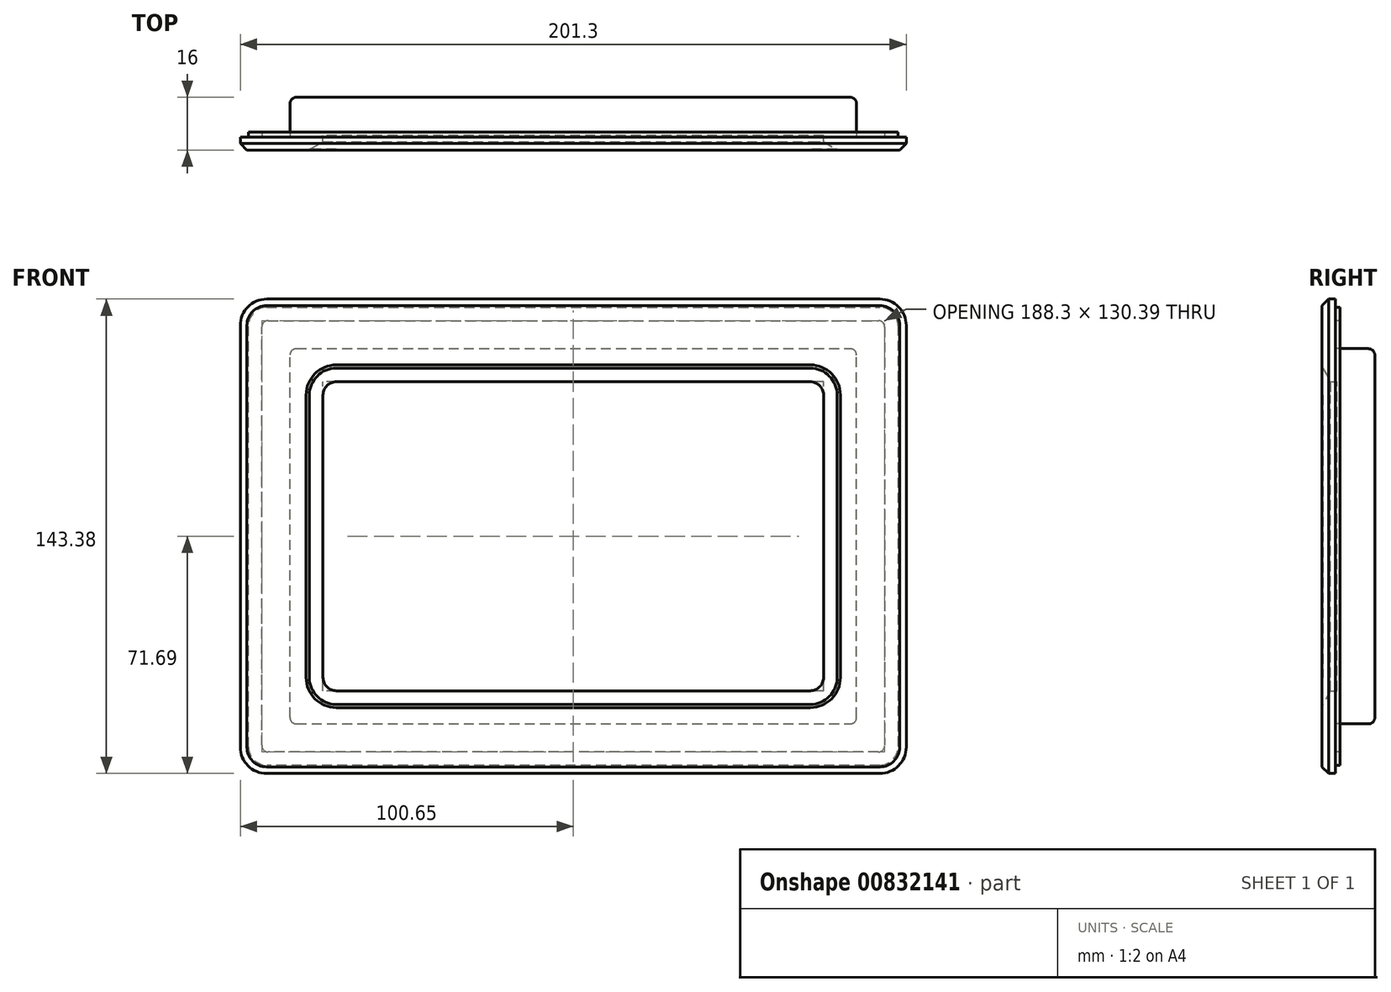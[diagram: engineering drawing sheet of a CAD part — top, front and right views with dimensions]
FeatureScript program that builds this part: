
annotation { "Feature Type Name" : "Feature", "Feature Type Description" : "" }
export const myFeature = defineFeature(function(context is Context, id is Id, definition is map)
    precondition{}
    {
        {
            var Q0;
            Q0=qCreatedBy(makeId("Front.planeOp"),FACE);
            var sketch = newSketch(context, id + "F0", { "sketchPlane" : qUnion([Q0])});
            skLineSegment(sketch, "E0.bottom", {"start": v(75.65, -46.7) * mm, "end": v(-75.65, -46.7) * mm});
            skLineSegment(sketch, "E0.top", {"start": v(75.65, 46.7) * mm, "end": v(-75.65, 46.7) * mm});
            skLineSegment(sketch, "E0.left", {"start": v(75.65, -46.7) * mm, "end": v(75.65, 46.7) * mm});
            skLineSegment(sketch, "E0.right", {"start": v(-75.65, -46.7) * mm, "end": v(-75.65, 46.7) * mm});
            skPoint(sketch, "E0.middle", {"position": v(0, 0) * mm});
            skSolve(sketch);
        }
        {
            var Q0;
            Q0 = qSketchRegion(id + "F0", true);
            extrude(context, id + "F1", {"entities" : qUnion([Q0]), "depth" : 0.5 * mm, "offsetDistance" : 25.4 * mm});
        }
        {
            var Q0;
            Q0=makeQuery(id+"F1.opExtrude","CAP_FACE",FACE,{"disambiguationData":[OSD([sQuery(id+"F0.wireOp",EDGE,"E0.bottom"),sQuery(id+"F0.wireOp",EDGE,"E0.top"),sQuery(id+"F0.wireOp",EDGE,"E0.left"),sQuery(id+"F0.wireOp",EDGE,"E0.right")])],"isStart":false});
            var sketch = newSketch(context, id + "F2", { "sketchPlane" : qUnion([Q0])});
            skLineSegment(sketch, "E1.bottom", {"start": v(-71.65, -46.7) * mm, "end": v(71.65, -46.7) * mm});
            skLineSegment(sketch, "E1.top", {"start": v(-71.65, 46.7) * mm, "end": v(71.65, 46.7) * mm});
            skLineSegment(sketch, "E1.left", {"start": v(-75.65, -42.7) * mm, "end": v(-75.65, 42.7) * mm});
            skLineSegment(sketch, "E1.right", {"start": v(75.65, -42.7) * mm, "end": v(75.65, 42.7) * mm});
            skPoint(sketch, "E1.middle", {"position": v(0, 0) * mm});
            skLineSegment(sketch, "E2.bottom", {"start": v(-92.65, -71.7) * mm, "end": v(92.65, -71.7) * mm});
            skLineSegment(sketch, "E2.top", {"start": v(-92.65, 71.7) * mm, "end": v(92.65, 71.7) * mm});
            skLineSegment(sketch, "E2.left", {"start": v(-100.65, -63.7) * mm, "end": v(-100.65, 63.7) * mm});
            skLineSegment(sketch, "E2.right", {"start": v(100.65, -63.7) * mm, "end": v(100.65, 63.7) * mm});
            skPoint(sketch, "E3.visualSharp", {"position": v(75.65, 46.7) * mm});
            skArc(sketch, "E3.filletArc", {"start": v(75.65, 42.7) * mm, "mid": v(74.48, 45.52) * mm, "end": v(71.65, 46.7) * mm});
            skPoint(sketch, "E4.visualSharp", {"position": v(75.65, -46.7) * mm});
            skArc(sketch, "E4.filletArc", {"start": v(71.65, -46.7) * mm, "mid": v(74.48, -45.52) * mm, "end": v(75.65, -42.7) * mm});
            skPoint(sketch, "E5.visualSharp", {"position": v(-75.65, -46.7) * mm});
            skArc(sketch, "E5.filletArc", {"start": v(-75.65, -42.7) * mm, "mid": v(-74.48, -45.52) * mm, "end": v(-71.65, -46.7) * mm});
            skPoint(sketch, "E6.visualSharp", {"position": v(-75.65, 46.7) * mm});
            skArc(sketch, "E6.filletArc", {"start": v(-71.65, 46.7) * mm, "mid": v(-74.48, 45.52) * mm, "end": v(-75.65, 42.7) * mm});
            skPoint(sketch, "E7.visualSharp", {"position": v(100.65, 71.7) * mm});
            skArc(sketch, "E7.filletArc", {"start": v(100.65, 63.7) * mm, "mid": v(98.3, 69.35) * mm, "end": v(92.65, 71.7) * mm});
            skPoint(sketch, "E8.visualSharp", {"position": v(100.65, -71.7) * mm});
            skArc(sketch, "E8.filletArc", {"start": v(92.65, -71.7) * mm, "mid": v(98.3, -69.35) * mm, "end": v(100.65, -63.7) * mm});
            skPoint(sketch, "E9.visualSharp", {"position": v(-100.65, -71.7) * mm});
            skArc(sketch, "E9.filletArc", {"start": v(-100.65, -63.7) * mm, "mid": v(-98.3, -69.35) * mm, "end": v(-92.65, -71.7) * mm});
            skPoint(sketch, "E10.visualSharp", {"position": v(-100.65, 71.7) * mm});
            skArc(sketch, "E10.filletArc", {"start": v(-92.65, 71.7) * mm, "mid": v(-98.3, 69.35) * mm, "end": v(-100.65, 63.7) * mm});
            skSolve(sketch);
        }
        {
            var Q0;
            {var subQ0=sQuery(id+"F2.wireOp",EDGE,"E1.bottom");Q0=makeQuery(id+"F2.imprint","IMPRINT",FACE,{"disambiguationData":[TD([[makeQuery(id+"F2.imprint","IMPRINT",EDGE,{"derivedFrom":subQ0}),1.0]])]});}
            var Q1;
            {var subQ0=sQuery(id+"F2.wireOp",EDGE,"E3.filletArc");Q1=makeQuery(id+"F2.imprint","IMPRINT",FACE,{"disambiguationData":[TD([[makeQuery(id+"F2.imprint","IMPRINT",EDGE,{"derivedFrom":subQ0}),-1.0]])]});}
            var Q2;
            {var subQ0=sQuery(id+"F2.wireOp",EDGE,"E5.filletArc");Q2=makeQuery(id+"F2.imprint","IMPRINT",FACE,{"disambiguationData":[TD([[makeQuery(id+"F2.imprint","IMPRINT",EDGE,{"derivedFrom":subQ0}),-1.0]])]});}
            var Q3;
            {var subQ0=sQuery(id+"F2.wireOp",EDGE,"E4.filletArc");Q3=makeQuery(id+"F2.imprint","IMPRINT",FACE,{"disambiguationData":[TD([[makeQuery(id+"F2.imprint","IMPRINT",EDGE,{"derivedFrom":subQ0}),-1.0]])]});}
            var Q4;
            {var subQ0=sQuery(id+"F2.wireOp",EDGE,"E6.filletArc");Q4=makeQuery(id+"F2.imprint","IMPRINT",FACE,{"disambiguationData":[TD([[makeQuery(id+"F2.imprint","IMPRINT",EDGE,{"derivedFrom":subQ0}),-1.0]])]});}
            extrude(context, id + "F3", {"entities" : qUnion([Q0, Q1, Q2, Q3, Q4]), "depth" : 4 * mm, "offsetDistance" : 25.4 * mm});
        }
        {
            var Q0;
            Q0=makeQuery(id+"F3.opExtrude","CAP_EDGE",EDGE,{"disambiguationData":[OSD([sQuery(id+"F2.wireOp",EDGE,"E1.left")])],"isStart":false});
            chamfer(context, id + "F4", {"entities" : qUnion([Q0]), "chamferType" : ChamferType.TWO_OFFSETS, "width1" : 4.57 * mm, "oppositeDirection" : false, "width2" : 2.54 * mm, "tangentPropagation" : true});
        }
        {
            var Q0;
            Q0=makeQuery(id+"F3.opExtrude","CAP_FACE",FACE,{"disambiguationData":[OSD([sQuery(id+"F2.wireOp",EDGE,"E1.bottom"),sQuery(id+"F2.wireOp",EDGE,"E1.top"),sQuery(id+"F2.wireOp",EDGE,"E1.left"),sQuery(id+"F2.wireOp",EDGE,"E1.right"),sQuery(id+"F2.wireOp",EDGE,"E2.bottom"),sQuery(id+"F2.wireOp",EDGE,"E2.top"),sQuery(id+"F2.wireOp",EDGE,"E2.left"),sQuery(id+"F2.wireOp",EDGE,"E2.right"),sQuery(id+"F2.wireOp",EDGE,"E3.filletArc"),sQuery(id+"F2.wireOp",EDGE,"E4.filletArc"),sQuery(id+"F2.wireOp",EDGE,"E5.filletArc"),sQuery(id+"F2.wireOp",EDGE,"E6.filletArc"),sQuery(id+"F2.wireOp",EDGE,"E7.filletArc"),sQuery(id+"F2.wireOp",EDGE,"E8.filletArc"),sQuery(id+"F2.wireOp",EDGE,"E9.filletArc"),sQuery(id+"F2.wireOp",EDGE,"E10.filletArc")])],"isStart":false});
            chamfer(context, id + "F5", {"entities" : qUnion([Q0]), "width" : 2 * mm, "tangentPropagation" : true});
        }
        {
            var Q0;
            Q0=makeQuery(id+"F3.opExtrude","CAP_FACE",FACE,{"disambiguationData":[OSD([sQuery(id+"F2.wireOp",EDGE,"E1.bottom"),sQuery(id+"F2.wireOp",EDGE,"E1.top"),sQuery(id+"F2.wireOp",EDGE,"E1.left"),sQuery(id+"F2.wireOp",EDGE,"E1.right"),sQuery(id+"F2.wireOp",EDGE,"E2.bottom"),sQuery(id+"F2.wireOp",EDGE,"E2.top"),sQuery(id+"F2.wireOp",EDGE,"E2.left"),sQuery(id+"F2.wireOp",EDGE,"E2.right"),sQuery(id+"F2.wireOp",EDGE,"E3.filletArc"),sQuery(id+"F2.wireOp",EDGE,"E4.filletArc"),sQuery(id+"F2.wireOp",EDGE,"E5.filletArc"),sQuery(id+"F2.wireOp",EDGE,"E6.filletArc"),sQuery(id+"F2.wireOp",EDGE,"E7.filletArc"),sQuery(id+"F2.wireOp",EDGE,"E8.filletArc"),sQuery(id+"F2.wireOp",EDGE,"E9.filletArc"),sQuery(id+"F2.wireOp",EDGE,"E10.filletArc")])],"isStart":true});
            var sketch = newSketch(context, id + "F6", { "sketchPlane" : qUnion([Q0])});
            skArc(sketch, "E11.0", {"start": v(98.15, 63.7) * mm, "mid": v(96.54, 67.58) * mm, "end": v(92.65, 69.2) * mm});
            skLineSegment(sketch, "E11.1", {"start": v(98.15, -63.7) * mm, "end": v(98.15, 63.7) * mm});
            skLineSegment(sketch, "E11.2", {"start": v(92.65, 69.2) * mm, "end": v(-92.65, 69.2) * mm});
            skArc(sketch, "E11.3", {"start": v(92.65, -69.2) * mm, "mid": v(96.54, -67.58) * mm, "end": v(98.15, -63.7) * mm});
            skArc(sketch, "E11.4", {"start": v(-92.65, 69.2) * mm, "mid": v(-96.54, 67.58) * mm, "end": v(-98.15, 63.7) * mm});
            skLineSegment(sketch, "E11.5", {"start": v(-98.15, 63.7) * mm, "end": v(-98.15, -63.7) * mm});
            skArc(sketch, "E11.6", {"start": v(-98.15, -63.7) * mm, "mid": v(-96.54, -67.58) * mm, "end": v(-92.65, -69.2) * mm});
            skLineSegment(sketch, "E11.7", {"start": v(-92.65, -69.2) * mm, "end": v(92.65, -69.2) * mm});
            skLineSegment(sketch, "E12.0", {"start": v(92.15, 65.2) * mm, "end": v(-92.15, 65.2) * mm});
            skLineSegment(sketch, "E12.1", {"start": v(94.15, -63.2) * mm, "end": v(94.15, 63.2) * mm});
            skLineSegment(sketch, "E12.2", {"start": v(-92.15, -65.2) * mm, "end": v(92.15, -65.2) * mm});
            skLineSegment(sketch, "E12.3", {"start": v(-94.15, 63.2) * mm, "end": v(-94.15, -63.2) * mm});
            skPoint(sketch, "E13.visualSharp", {"position": v(94.15, -65.2) * mm});
            skArc(sketch, "E13.filletArc", {"start": v(92.15, -65.2) * mm, "mid": v(93.56, -64.6) * mm, "end": v(94.15, -63.2) * mm});
            skPoint(sketch, "E14.visualSharp", {"position": v(94.15, 65.2) * mm});
            skArc(sketch, "E14.filletArc", {"start": v(94.15, 63.2) * mm, "mid": v(93.56, 64.6) * mm, "end": v(92.15, 65.2) * mm});
            skPoint(sketch, "E15.visualSharp", {"position": v(-94.15, 65.2) * mm});
            skArc(sketch, "E15.filletArc", {"start": v(-92.15, 65.2) * mm, "mid": v(-93.56, 64.6) * mm, "end": v(-94.15, 63.2) * mm});
            skPoint(sketch, "E16.visualSharp", {"position": v(-94.15, -65.2) * mm});
            skArc(sketch, "E16.filletArc", {"start": v(-94.15, -63.2) * mm, "mid": v(-93.56, -64.6) * mm, "end": v(-92.15, -65.2) * mm});
            skSolve(sketch);
        }
        {
            var Q0;
            Q0=makeQuery(id+"F6.imprint","IMPRINT",FACE,{"disambiguationData":[TD([[makeQuery(id+"F6.imprint","IMPRINT",EDGE,{"derivedFrom":sQuery(id+"F6.wireOp",EDGE,"E11.0")}),1.0]])]});
            extrude(context, id + "F7", {"entities" : qUnion([Q0]), "depth" : 1.5 * mm, "offsetDistance" : 25.4 * mm});
        }
        {
            var Q0;
            Q0=makeQuery(id+"F3.opExtrude","CAP_FACE",FACE,{"disambiguationData":[OSD([sQuery(id+"F2.wireOp",EDGE,"E1.bottom"),sQuery(id+"F2.wireOp",EDGE,"E1.top"),sQuery(id+"F2.wireOp",EDGE,"E1.left"),sQuery(id+"F2.wireOp",EDGE,"E1.right"),sQuery(id+"F2.wireOp",EDGE,"E2.bottom"),sQuery(id+"F2.wireOp",EDGE,"E2.top"),sQuery(id+"F2.wireOp",EDGE,"E2.left"),sQuery(id+"F2.wireOp",EDGE,"E2.right"),sQuery(id+"F2.wireOp",EDGE,"E3.filletArc"),sQuery(id+"F2.wireOp",EDGE,"E4.filletArc"),sQuery(id+"F2.wireOp",EDGE,"E5.filletArc"),sQuery(id+"F2.wireOp",EDGE,"E6.filletArc"),sQuery(id+"F2.wireOp",EDGE,"E7.filletArc"),sQuery(id+"F2.wireOp",EDGE,"E8.filletArc"),sQuery(id+"F2.wireOp",EDGE,"E9.filletArc"),sQuery(id+"F2.wireOp",EDGE,"E10.filletArc")])],"isStart":true});
            var sketch = newSketch(context, id + "F8", { "sketchPlane" : qUnion([Q0])});
            skLineSegment(sketch, "E17.1", {"start": v(85.65, -56.7) * mm, "end": v(85.65, 56.7) * mm});
            skLineSegment(sketch, "E17.2", {"start": v(85.65, 56.7) * mm, "end": v(-85.65, 56.7) * mm});
            skLineSegment(sketch, "E17.5", {"start": v(-85.65, -56.7) * mm, "end": v(-85.65, 56.7) * mm});
            skLineSegment(sketch, "E17.7", {"start": v(85.65, -56.7) * mm, "end": v(-85.65, -56.7) * mm});
            skSolve(sketch);
        }
        {
            var Q0;
            Q0 = qSketchRegion(id + "F8", true);
            extrude(context, id + "F9", {"entities" : qUnion([Q0]), "depth" : 12 * mm, "offsetDistance" : 25.4 * mm});
        }
        {
            var Q0;
            Q0=makeQuery(id+"F9.opExtrude","CAP_EDGE",EDGE,{"disambiguationData":[OSD([sQuery(id+"F8.wireOp",EDGE,"E17.2")])],"isStart":false});
            var Q1;
            Q1=makeQuery(id+"F9.opExtrude","CAP_EDGE",EDGE,{"disambiguationData":[OSD([sQuery(id+"F8.wireOp",EDGE,"E17.1")])],"isStart":false});
            var Q2;
            Q2=makeQuery(id+"F9.opExtrude","SWEPT_EDGE",EDGE,{"disambiguationData":[OSD([sQuery(id+"F8.wireOp",EDGE,"E17.1"),sQuery(id+"F8.wireOp",EDGE,"E17.2")])]});
            var Q3;
            Q3=makeQuery(id+"F9.opExtrude","SWEPT_EDGE",EDGE,{"disambiguationData":[OSD([sQuery(id+"F8.wireOp",EDGE,"E17.2"),sQuery(id+"F8.wireOp",EDGE,"E17.5")])]});
            var Q4;
            Q4=makeQuery(id+"F9.opExtrude","CAP_EDGE",EDGE,{"disambiguationData":[OSD([sQuery(id+"F8.wireOp",EDGE,"E17.5")])],"isStart":false});
            var Q5;
            Q5=makeQuery(id+"F9.opExtrude","SWEPT_EDGE",EDGE,{"disambiguationData":[OSD([sQuery(id+"F8.wireOp",EDGE,"E17.5"),sQuery(id+"F8.wireOp",EDGE,"E17.7")])]});
            var Q6;
            Q6=makeQuery(id+"F9.opExtrude","CAP_EDGE",EDGE,{"disambiguationData":[OSD([sQuery(id+"F8.wireOp",EDGE,"E17.7")])],"isStart":false});
            var Q7;
            Q7=makeQuery(id+"F9.opExtrude","SWEPT_EDGE",EDGE,{"disambiguationData":[OSD([sQuery(id+"F8.wireOp",EDGE,"E17.1"),sQuery(id+"F8.wireOp",EDGE,"E17.7")])]});
            fillet(context, id + "F10", {"entities" : qUnion([Q0, Q1, Q2, Q3, Q4, Q5, Q6, Q7]), "radius" : 2 * mm, "tangentPropagation" : true, "allowEdgeOverflow" : false});
        }
    });
